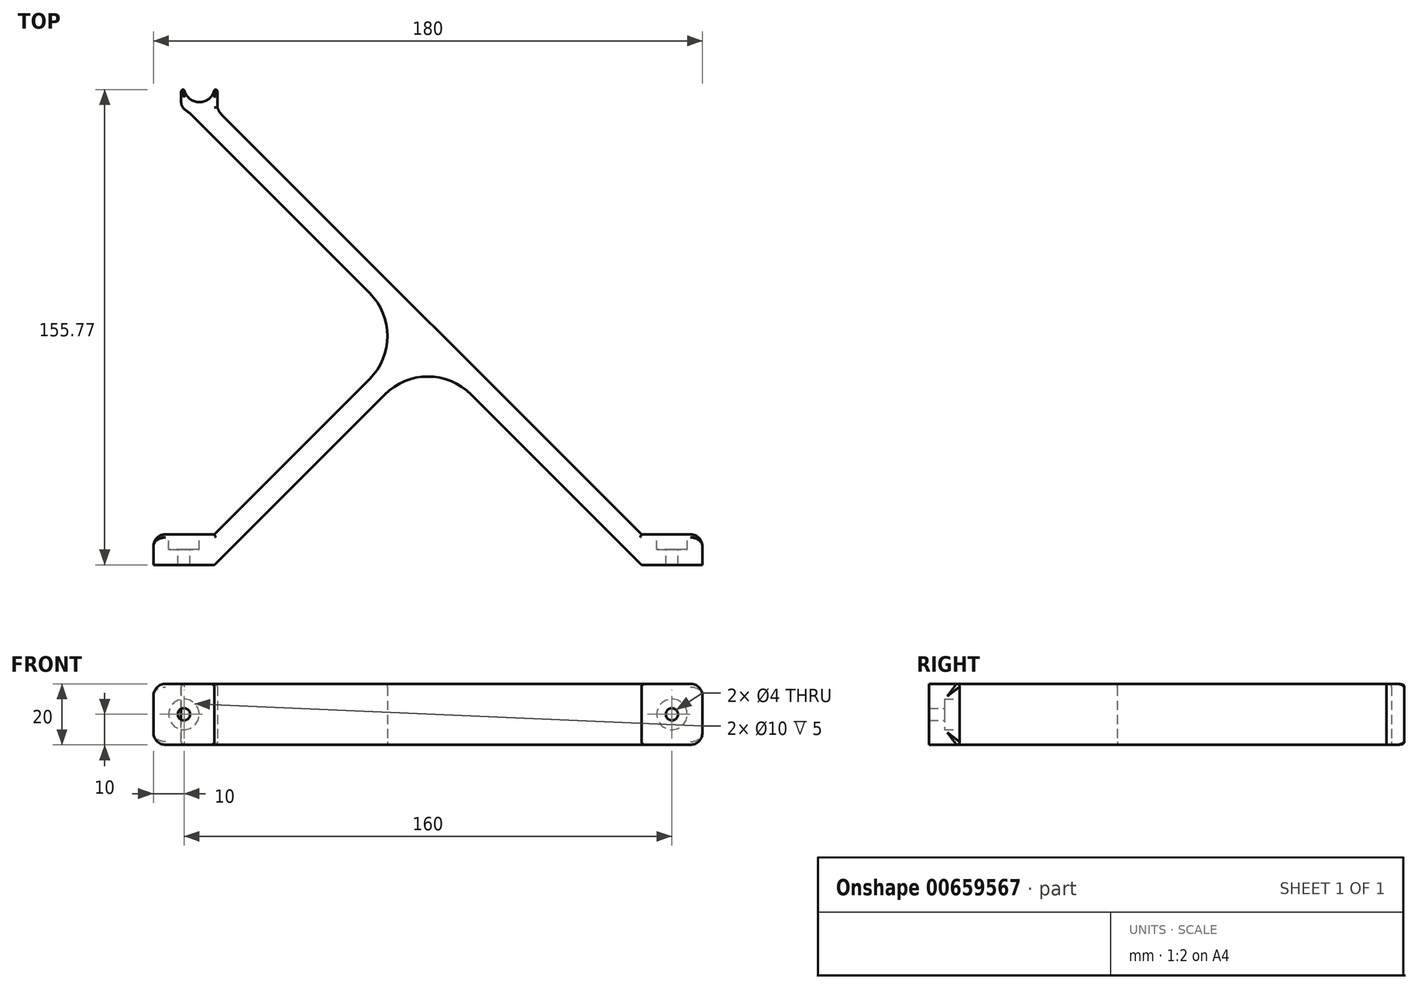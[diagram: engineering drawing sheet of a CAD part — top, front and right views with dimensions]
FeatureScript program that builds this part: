
annotation { "Feature Type Name" : "Feature", "Feature Type Description" : "" }
export const myFeature = defineFeature(function(context is Context, id is Id, definition is map)
    precondition{}
    {
        {
            var Q0;
            Q0=qCreatedBy(makeId("Top.planeOp"),FACE);
            var sketch = newSketch(context, id + "F0", { "sketchPlane" : qUnion([Q0])});
            skLineSegment(sketch, "E0", {"start": v(0, 0) * mm, "end": v(0, -75) * mm, "construction": true});
            skLineSegment(sketch, "E1", {"start": v(0, -75) * mm, "end": v(75, -75) * mm, "construction": true});
            skLineSegment(sketch, "E2", {"start": v(75, -75) * mm, "end": v(-74.9, 74.9) * mm});
            skLineSegment(sketch, "E3", {"start": v(0, 0) * mm, "end": v(-75, -75) * mm});
            skLineSegment(sketch, "E4", {"start": v(-147, -24.26) * mm, "end": v(-137, -24.26) * mm});
            skPoint(sketch, "E5", {"position": v(-142, -24.26) * mm});
            skLineSegment(sketch, "E6", {"start": v(-80, -75) * mm, "end": v(-70, -75) * mm});
            skPoint(sketch, "E7", {"position": v(-75, -75) * mm});
            skLineSegment(sketch, "E8", {"start": v(70, -75) * mm, "end": v(80, -75) * mm});
            skPoint(sketch, "E9", {"position": v(75, -75) * mm});
            skLineSegment(sketch, "E10", {"start": v(-5, -5) * mm, "end": v(5, -5) * mm});
            skPoint(sketch, "E11", {"position": v(0, -5) * mm});
            skLineSegment(sketch, "E12", {"start": v(-70, -75) * mm, "end": v(0, -5) * mm});
            skLineSegment(sketch, "E13", {"start": v(0, -5) * mm, "end": v(70, -75) * mm});
            skLineSegment(sketch, "E14", {"start": v(-5, 5) * mm, "end": v(-5, -5) * mm});
            skPoint(sketch, "E15", {"position": v(-5, 0) * mm});
            skLineSegment(sketch, "E16", {"start": v(-80, -75) * mm, "end": v(-5, 0) * mm});
            skLineSegment(sketch, "E17", {"start": v(80, -75) * mm, "end": v(-70, 75) * mm});
            skLineSegment(sketch, "E18", {"start": v(-70, 75) * mm, "end": v(-74.9, 74.9) * mm});
            skLineSegment(sketch, "E19", {"start": v(-74.9, 74.9) * mm, "end": v(-79.9, 74.9) * mm});
            skLineSegment(sketch, "E20", {"start": v(-79.9, 74.9) * mm, "end": v(-5, 0) * mm});
            skLineSegment(sketch, "E21", {"start": v(-5, 0) * mm, "end": v(-19.14, 14.14) * mm, "construction": true});
            skLineSegment(sketch, "E22", {"start": v(-5, 0) * mm, "end": v(-19.14, -14.14) * mm, "construction": true});
            skArc(sketch, "E23", {"start": v(-19.14, -14.14) * mm, "mid": v(-13.28, 0) * mm, "end": v(-19.14, 14.14) * mm});
            skLineSegment(sketch, "E24", {"start": v(0, -5) * mm, "end": v(-14.14, -19.14) * mm, "construction": true});
            skLineSegment(sketch, "E25", {"start": v(0, -5) * mm, "end": v(14.14, -19.14) * mm, "construction": true});
            skArc(sketch, "E26", {"start": v(14.14, -19.14) * mm, "mid": v(0, -13.28) * mm, "end": v(-14.14, -19.14) * mm});
            skLineSegment(sketch, "E27.bottom", {"start": v(-70, -75) * mm, "end": v(-90, -75) * mm});
            skLineSegment(sketch, "E27.top", {"start": v(-70, -65) * mm, "end": v(-90, -65) * mm});
            skLineSegment(sketch, "E27.left", {"start": v(-70, -75) * mm, "end": v(-70, -65) * mm});
            skLineSegment(sketch, "E27.right", {"start": v(-90, -75) * mm, "end": v(-90, -65) * mm});
            skLineSegment(sketch, "E28.bottom", {"start": v(70, -75) * mm, "end": v(90, -75) * mm});
            skLineSegment(sketch, "E28.top", {"start": v(70, -65) * mm, "end": v(90, -65) * mm});
            skLineSegment(sketch, "E28.left", {"start": v(70, -75) * mm, "end": v(70, -65) * mm});
            skLineSegment(sketch, "E28.right", {"start": v(90, -75) * mm, "end": v(90, -65) * mm});
            skArc(sketch, "E29", {"start": v(-79.9, 80.98) * mm, "mid": v(-74.95, 76.66) * mm, "end": v(-70, 80.98) * mm});
            skLineSegment(sketch, "E30", {"start": v(-79.9, 80.98) * mm, "end": v(-79.9, 74.9) * mm});
            skLineSegment(sketch, "E31", {"start": v(-70, 80.98) * mm, "end": v(-70, 75) * mm});
            skLineSegment(sketch, "E32", {"start": v(-79.9, 74.9) * mm, "end": v(-80.9, 74.9) * mm});
            skLineSegment(sketch, "E33", {"start": v(-80.9, 74.9) * mm, "end": v(-80.9, 80.98) * mm});
            skLineSegment(sketch, "E34", {"start": v(-79.9, 80.98) * mm, "end": v(-80.9, 80.98) * mm});
            skLineSegment(sketch, "E35", {"start": v(-70, 75) * mm, "end": v(-69, 75) * mm});
            skLineSegment(sketch, "E36", {"start": v(-69, 75) * mm, "end": v(-69, 80.98) * mm});
            skLineSegment(sketch, "E37", {"start": v(-69, 80.98) * mm, "end": v(-70, 80.98) * mm});
            skSolve(sketch);
        }
        {
            var Q0;
            {var subQ5=sQuery(id+"F0.wireOp",EDGE,"E12");Q0=makeQuery(id+"F0.imprint","IMPRINT",FACE,{"disambiguationData":[TD([[makeQuery(id+"F0.imprint","IMPRINT",EDGE,{"derivedFrom":subQ5}),1.0]])]});}
            var Q1;
            {var subQ5=sQuery(id+"F0.wireOp",EDGE,"E16");Q1=makeQuery(id+"F0.imprint","IMPRINT",FACE,{"disambiguationData":[TD([[makeQuery(id+"F0.imprint","IMPRINT",EDGE,{"derivedFrom":subQ5}),-1.0]])]});}
            var Q2;
            {var subQ5=sQuery(id+"F0.wireOp",EDGE,"E13");Q2=makeQuery(id+"F0.imprint","IMPRINT",FACE,{"disambiguationData":[TD([[makeQuery(id+"F0.imprint","IMPRINT",EDGE,{"derivedFrom":subQ5}),1.0]])]});}
            var Q3;
            {var subQ7=sQuery(id+"F0.wireOp",EDGE,"E17");Q3=makeQuery(id+"F0.imprint","IMPRINT",FACE,{"disambiguationData":[TD([[makeQuery(id+"F0.imprint","IMPRINT",EDGE,{"derivedFrom":subQ7}),1.0]])]});}
            var Q4;
            {var subQ0=sQuery(id+"F0.wireOp",EDGE,"E19");Q4=makeQuery(id+"F0.imprint","IMPRINT",FACE,{"disambiguationData":[TD([[makeQuery(id+"F0.imprint","IMPRINT",EDGE,{"derivedFrom":subQ0}),1.0]])]});}
            var Q5;
            {var subQ0=sQuery(id+"F0.wireOp",EDGE,"E3");var subQ1=sQuery(id+"F0.wireOp",EDGE,"E2");var subQ2=makeQuery(id+"F0.imprint","INTERSECT",VERTEX,{"derivedFrom":[subQ1,subQ0]});Q5=makeQuery(id+"F0.imprint","IMPRINT",FACE,{"disambiguationData":[TD([[makeQuery(id+"F0.imprint","IMPRINT",EDGE,{"disambiguationData":[TD([[subQ2,-1.0]])],"derivedFrom":subQ1}),1.0]])]});}
            var Q6;
            {var subQ0=sQuery(id+"F0.wireOp",EDGE,"E3");var subQ1=sQuery(id+"F0.wireOp",EDGE,"E2");var subQ2=makeQuery(id+"F0.imprint","INTERSECT",VERTEX,{"derivedFrom":[subQ1,subQ0]});Q6=makeQuery(id+"F0.imprint","IMPRINT",FACE,{"disambiguationData":[TD([[makeQuery(id+"F0.imprint","IMPRINT",EDGE,{"disambiguationData":[TD([[subQ2,1.0]])],"derivedFrom":subQ1}),1.0]])]});}
            var Q7;
            {var subQ3=sQuery(id+"F0.wireOp",EDGE,"E26");Q7=makeQuery(id+"F0.imprint","IMPRINT",FACE,{"disambiguationData":[TD([[makeQuery(id+"F0.imprint","IMPRINT",EDGE,{"derivedFrom":subQ3}),-1.0]])]});}
            var Q8;
            {var subQ3=sQuery(id+"F0.wireOp",EDGE,"E23");Q8=makeQuery(id+"F0.imprint","IMPRINT",FACE,{"disambiguationData":[TD([[makeQuery(id+"F0.imprint","IMPRINT",EDGE,{"derivedFrom":subQ3}),-1.0]])]});}
            var Q9;
            {var subQ3=sQuery(id+"F0.wireOp",EDGE,"E28.top");Q9=makeQuery(id+"F0.imprint","IMPRINT",FACE,{"disambiguationData":[TD([[makeQuery(id+"F0.imprint","IMPRINT",EDGE,{"derivedFrom":subQ3}),-1.0]])]});}
            var Q10;
            {var subQ0=sQuery(id+"F0.wireOp",EDGE,"E28.bottom");var subQ1=sQuery(id+"F0.wireOp",EDGE,"E2");var subQ2=makeQuery(id+"F0.imprint","INTERSECT",VERTEX,{"derivedFrom":[subQ1,subQ0]});Q10=makeQuery(id+"F0.imprint","IMPRINT",FACE,{"disambiguationData":[TD([[makeQuery(id+"F0.imprint","IMPRINT",EDGE,{"disambiguationData":[TD([[subQ2,-1.0]])],"derivedFrom":subQ1}),1.0]])]});}
            var Q11;
            {var subQ0=sQuery(id+"F0.wireOp",EDGE,"E18");Q11=makeQuery(id+"F0.imprint","IMPRINT",FACE,{"disambiguationData":[TD([[makeQuery(id+"F0.imprint","IMPRINT",EDGE,{"derivedFrom":subQ0}),1.0]])]});}
            var Q12;
            {var subQ0=sQuery(id+"F0.wireOp",EDGE,"E27.bottom");var subQ1=sQuery(id+"F0.wireOp",EDGE,"E3");var subQ2=makeQuery(id+"F0.imprint","INTERSECT",VERTEX,{"derivedFrom":[subQ1,subQ0]});Q12=makeQuery(id+"F0.imprint","IMPRINT",FACE,{"disambiguationData":[TD([[makeQuery(id+"F0.imprint","IMPRINT",EDGE,{"disambiguationData":[TD([[subQ2,1.0]])],"derivedFrom":subQ1}),-1.0]])]});}
            var Q13;
            {var subQ0=sQuery(id+"F0.wireOp",EDGE,"E27.bottom");var subQ1=sQuery(id+"F0.wireOp",EDGE,"E3");var subQ2=makeQuery(id+"F0.imprint","INTERSECT",VERTEX,{"derivedFrom":[subQ1,subQ0]});Q13=makeQuery(id+"F0.imprint","IMPRINT",FACE,{"disambiguationData":[TD([[makeQuery(id+"F0.imprint","IMPRINT",EDGE,{"disambiguationData":[TD([[subQ2,1.0]])],"derivedFrom":subQ1}),1.0]])]});}
            var Q14;
            {var subQ3=sQuery(id+"F0.wireOp",EDGE,"E27.top");Q14=makeQuery(id+"F0.imprint","IMPRINT",FACE,{"disambiguationData":[TD([[makeQuery(id+"F0.imprint","IMPRINT",EDGE,{"derivedFrom":subQ3}),1.0]])]});}
            var Q15;
            Q15=makeQuery(id+"F0.imprint","IMPRINT",FACE,{"disambiguationData":[TD([[makeQuery(id+"F0.imprint","IMPRINT",EDGE,{"derivedFrom":sQuery(id+"F0.wireOp",EDGE,"E18")}),-1.0]])]});
            var Q16;
            Q16=makeQuery(id+"F0.imprint","IMPRINT",FACE,{"disambiguationData":[TD([[makeQuery(id+"F0.imprint","IMPRINT",EDGE,{"derivedFrom":sQuery(id+"F0.wireOp",EDGE,"E30")}),-1.0]])]});
            var Q17;
            Q17=makeQuery(id+"F0.imprint","IMPRINT",FACE,{"disambiguationData":[TD([[makeQuery(id+"F0.imprint","IMPRINT",EDGE,{"derivedFrom":sQuery(id+"F0.wireOp",EDGE,"E31")}),1.0]])]});
            extrude(context, id + "F1", {"entities" : qUnion([Q0, Q1, Q2, Q3, Q4, Q5, Q6, Q7, Q8, Q9, Q10, Q11, Q12, Q13, Q14, Q15, Q16, Q17]), "endBound" : BoundingType.SYMMETRIC, "depth" : 20 * mm});
        }
        {
            var Q0;
            Q0=makeQuery(id+"F1.opExtrude","SWEPT_EDGE",EDGE,{"disambiguationData":[OSD([sQuery(id+"F0.wireOp",EDGE,"E19"),sQuery(id+"F0.wireOp",EDGE,"E20"),sQuery(id+"F0.wireOp",EDGE,"E30"),sQuery(id+"F0.wireOp",EDGE,"E32")])]});
            fillet(context, id + "F2", {"entities" : qUnion([Q0]), "radius" : 15 * mm, "tangentPropagation" : true, "allowEdgeOverflow" : false});
        }
        {
            var Q0;
            Q0=makeQuery(id+"F1.opExtrude","SWEPT_EDGE",EDGE,{"disambiguationData":[OSD([sQuery(id+"F0.wireOp",EDGE,"E17"),sQuery(id+"F0.wireOp",EDGE,"E18"),sQuery(id+"F0.wireOp",EDGE,"E31"),sQuery(id+"F0.wireOp",EDGE,"E35")])]});
            fillet(context, id + "F3", {"entities" : qUnion([Q0]), "radius" : 5 * mm, "tangentPropagation" : true, "allowEdgeOverflow" : false});
        }
        {
            var Q0;
            Q0=makeQuery(id+"F2.opFillet","BLEND_EDGE",EDGE,{"blendedFrom":[makeQuery(id+"F1.opExtrude","SWEPT_EDGE",EDGE,{"disambiguationData":[OSD([sQuery(id+"F0.wireOp",EDGE,"E19"),sQuery(id+"F0.wireOp",EDGE,"E20"),sQuery(id+"F0.wireOp",EDGE,"E30"),sQuery(id+"F0.wireOp",EDGE,"E32")])]}),makeQuery(id+"F1.opExtrude","SWEPT_FACE",FACE,{"disambiguationData":[OSD([sQuery(id+"F0.wireOp",EDGE,"E33")])]})],"blendedInto":[makeQuery(id+"F1.opExtrude","SWEPT_FACE",FACE,{"disambiguationData":[OSD([sQuery(id+"F0.wireOp",EDGE,"E33")])]})]});
            fillet(context, id + "F4", {"entities" : qUnion([Q0]), "radius" : 3 * mm, "tangentPropagation" : true, "allowEdgeOverflow" : false});
        }
        {
            var Q0;
            Q0=makeQuery(id+"F1.opExtrude","SWEPT_FACE",FACE,{"disambiguationData":[OSD([sQuery(id+"F0.wireOp",EDGE,"E27.top")])]});
            var sketch = newSketch(context, id + "F5", { "sketchPlane" : qUnion([Q0])});
            skPoint(sketch, "E38", {"position": v(80, 0) * mm});
            skPoint(sketch, "E38.positionSnap0", {"position": v(80, -10) * mm});
            skPoint(sketch, "E38.positionSnap1", {"position": v(90, 0) * mm});
            skCircle(sketch, "E39", {"center": v(80, 0) * mm, "radius": 5 * mm});
            skCircle(sketch, "E40", {"center": v(80, 0) * mm, "radius": 2 * mm});
            skSolve(sketch);
        }
        {
            var Q0;
            Q0=makeQuery(id+"F1.opExtrude","SWEPT_FACE",FACE,{"disambiguationData":[OSD([sQuery(id+"F0.wireOp",EDGE,"E28.top")])]});
            var sketch = newSketch(context, id + "F6", { "sketchPlane" : qUnion([Q0])});
            skPoint(sketch, "E41", {"position": v(-80, 0) * mm});
            skPoint(sketch, "E41.positionSnap0", {"position": v(-80, 10) * mm});
            skPoint(sketch, "E41.positionSnap1", {"position": v(-70, 0) * mm});
            skPoint(sketch, "E42.positionSnap0", {"position": v(-80, -8.37) * mm});
            skPoint(sketch, "E42.positionSnap1", {"position": v(-77.63, 0) * mm});
            skCircle(sketch, "E43", {"center": v(-80, 0) * mm, "radius": 5 * mm});
            skCircle(sketch, "E44", {"center": v(-80, 0) * mm, "radius": 2 * mm});
            skSolve(sketch);
        }
        {
            var Q0;
            Q0=makeQuery(id+"F5.imprint","IMPRINT",FACE,{"disambiguationData":[TD([[makeQuery(id+"F5.imprint","IMPRINT",EDGE,{"derivedFrom":sQuery(id+"F5.wireOp",EDGE,"E40")}),1.0]])]});
            var Q1;
            Q1=makeQuery(id+"F6.imprint","IMPRINT",FACE,{"disambiguationData":[TD([[makeQuery(id+"F6.imprint","IMPRINT",EDGE,{"derivedFrom":sQuery(id+"F6.wireOp",EDGE,"E44")}),1.0]])]});
            extrude(context, id + "F7", {"entities" : qUnion([Q0, Q1]), "operationType" : NewBodyOperationType.REMOVE, "oppositeDirection" : true, "depth" : 25 * mm});
        }
        {
            var Q0;
            Q0=makeQuery(id+"F5.imprint","IMPRINT",FACE,{"disambiguationData":[TD([[makeQuery(id+"F5.imprint","IMPRINT",EDGE,{"derivedFrom":sQuery(id+"F5.wireOp",EDGE,"E39")}),1.0]])]});
            var Q1;
            Q1=qSketchRegion(id+"F6",true);
            extrude(context, id + "F8", {"entities" : qUnion([Q0, Q1]), "operationType" : NewBodyOperationType.REMOVE, "oppositeDirection" : true, "depth" : 5 * mm});
        }
        {
            var Q0;
            Q0=makeQuery(id+"F1.opExtrude","SWEPT_EDGE",EDGE,{"disambiguationData":[OSD([sQuery(id+"F0.wireOp",EDGE,"E27.top"),sQuery(id+"F0.wireOp",EDGE,"E27.right")])]});
            var Q1;
            Q1=makeQuery(id+"F1.opExtrude","CAP_EDGE",EDGE,{"disambiguationData":[OSD([sQuery(id+"F0.wireOp",EDGE,"E27.right")])],"isStart":false});
            var Q2;
            Q2=makeQuery(id+"F1.opExtrude","CAP_EDGE",EDGE,{"disambiguationData":[OSD([sQuery(id+"F0.wireOp",EDGE,"E27.right")])],"isStart":true});
            var Q3;
            Q3=makeQuery(id+"F1.opExtrude","CAP_EDGE",EDGE,{"disambiguationData":[OSD([sQuery(id+"F0.wireOp",EDGE,"E28.right")])],"isStart":false});
            var Q4;
            Q4=makeQuery(id+"F1.opExtrude","CAP_EDGE",EDGE,{"disambiguationData":[OSD([sQuery(id+"F0.wireOp",EDGE,"E28.right")])],"isStart":true});
            var Q5;
            Q5=makeQuery(id+"F1.opExtrude","SWEPT_EDGE",EDGE,{"disambiguationData":[OSD([sQuery(id+"F0.wireOp",EDGE,"E28.top"),sQuery(id+"F0.wireOp",EDGE,"E28.right")])]});
            fillet(context, id + "F9", {"entities" : qUnion([Q0, Q1, Q2, Q3, Q4, Q5]), "radius" : 4 * mm, "tangentPropagation" : true, "allowEdgeOverflow" : false});
        }
        {
            var Q0;
            Q0=makeQuery(id+"F1.opExtrude","CAP_EDGE",EDGE,{"disambiguationData":[OSD([sQuery(id+"F0.wireOp",EDGE,"E28.top")])],"isStart":true});
            var Q1;
            Q1=makeQuery(id+"F1.opExtrude","CAP_EDGE",EDGE,{"disambiguationData":[OSD([sQuery(id+"F0.wireOp",EDGE,"E28.top")])],"isStart":false});
            var Q2;
            Q2=makeQuery(id+"F1.opExtrude","CAP_EDGE",EDGE,{"disambiguationData":[OSD([sQuery(id+"F0.wireOp",EDGE,"E17")])],"isStart":true});
            var Q3;
            Q3=makeQuery(id+"F1.opExtrude","CAP_EDGE",EDGE,{"disambiguationData":[OSD([sQuery(id+"F0.wireOp",EDGE,"E17")])],"isStart":false});
            var Q4;
            Q4=makeQuery(id+"F1.opExtrude","CAP_EDGE",EDGE,{"disambiguationData":[OSD([sQuery(id+"F0.wireOp",EDGE,"E27.top")])],"isStart":true});
            var Q5;
            Q5=makeQuery(id+"F1.opExtrude","CAP_EDGE",EDGE,{"disambiguationData":[OSD([sQuery(id+"F0.wireOp",EDGE,"E27.top")])],"isStart":false});
            var Q6;
            Q6=makeQuery(id+"F1.opExtrude","CAP_EDGE",EDGE,{"disambiguationData":[OSD([sQuery(id+"F0.wireOp",EDGE,"E13")])],"isStart":true});
            var Q7;
            Q7=makeQuery(id+"F1.opExtrude","CAP_EDGE",EDGE,{"disambiguationData":[OSD([sQuery(id+"F0.wireOp",EDGE,"E13")])],"isStart":false});
            fillet(context, id + "F10", {"entities" : qUnion([Q0, Q1, Q2, Q3, Q4, Q5, Q6, Q7]), "radius" : 1 * mm, "tangentPropagation" : true, "allowEdgeOverflow" : false});
        }
        {
            var Q0;
            Q0=makeQuery(id+"F1.opExtrude","SWEPT_EDGE",EDGE,{"disambiguationData":[OSD([sQuery(id+"F0.wireOp",EDGE,"E29"),sQuery(id+"F0.wireOp",EDGE,"E31"),sQuery(id+"F0.wireOp",EDGE,"E37")])]});
            var Q1;
            Q1=makeQuery(id+"F1.opExtrude","SWEPT_EDGE",EDGE,{"disambiguationData":[OSD([sQuery(id+"F0.wireOp",EDGE,"E36"),sQuery(id+"F0.wireOp",EDGE,"E37")])]});
            var Q2;
            Q2=makeQuery(id+"F1.opExtrude","SWEPT_EDGE",EDGE,{"disambiguationData":[OSD([sQuery(id+"F0.wireOp",EDGE,"E29"),sQuery(id+"F0.wireOp",EDGE,"E30"),sQuery(id+"F0.wireOp",EDGE,"E34")])]});
            var Q3;
            Q3=makeQuery(id+"F1.opExtrude","SWEPT_EDGE",EDGE,{"disambiguationData":[OSD([sQuery(id+"F0.wireOp",EDGE,"E33"),sQuery(id+"F0.wireOp",EDGE,"E34")])]});
            fillet(context, id + "F11", {"entities" : qUnion([Q0, Q1, Q2, Q3]), "radius" : 1 * mm, "tangentPropagation" : true, "allowEdgeOverflow" : false});
        }
        {
            var Q0;
            {var subQ0=sQuery(id+"F0.wireOp",EDGE,"E37");Q0=makeQuery(id+"F11.opFillet","BLEND_EDGE",EDGE,{"blendedFrom":[makeQuery(id+"F1.opExtrude","SWEPT_EDGE",EDGE,{"disambiguationData":[OSD([sQuery(id+"F0.wireOp",EDGE,"E29"),sQuery(id+"F0.wireOp",EDGE,"E31"),subQ0])]}),makeQuery(id+"F1.opExtrude","SWEPT_EDGE",EDGE,{"disambiguationData":[OSD([sQuery(id+"F0.wireOp",EDGE,"E36"),subQ0])]})],"blendedInto":[]});}
            var Q1;
            {var subQ0=sQuery(id+"F0.wireOp",EDGE,"E34");Q1=makeQuery(id+"F11.opFillet","BLEND_EDGE",EDGE,{"blendedFrom":[makeQuery(id+"F1.opExtrude","SWEPT_EDGE",EDGE,{"disambiguationData":[OSD([sQuery(id+"F0.wireOp",EDGE,"E29"),sQuery(id+"F0.wireOp",EDGE,"E30"),subQ0])]}),makeQuery(id+"F1.opExtrude","SWEPT_EDGE",EDGE,{"disambiguationData":[OSD([sQuery(id+"F0.wireOp",EDGE,"E33"),subQ0])]})],"blendedInto":[]});}
            fillet(context, id + "F12", {"entities" : qUnion([Q0, Q1]), "radius" : .5 * mm, "tangentPropagation" : true, "allowEdgeOverflow" : false});
        }
        {
            var Q0;
            Q0=makeQuery(id+"F1.opExtrude","CAP_EDGE",EDGE,{"disambiguationData":[OSD([sQuery(id+"F0.wireOp",EDGE,"E36")])],"isStart":true});
            var Q1;
            Q1=makeQuery(id+"F1.opExtrude","CAP_EDGE",EDGE,{"disambiguationData":[OSD([sQuery(id+"F0.wireOp",EDGE,"E36")])],"isStart":false});
            var Q2;
            Q2=makeQuery(id+"F1.opExtrude","CAP_EDGE",EDGE,{"disambiguationData":[OSD([sQuery(id+"F0.wireOp",EDGE,"E33")])],"isStart":true});
            var Q3;
            {var subQ0=sQuery(id+"F0.wireOp",EDGE,"E33");var subQ1=sQuery(id+"F0.wireOp",EDGE,"E32");var subQ2=sQuery(id+"F0.wireOp",EDGE,"E20");Q3=makeQuery(id+"F4.opFillet","BLEND_EDGE",EDGE,{"blendedFrom":[makeQuery(id+"F2.opFillet","BLEND_EDGE",EDGE,{"blendedFrom":[makeQuery(id+"F1.opExtrude","SWEPT_EDGE",EDGE,{"disambiguationData":[OSD([sQuery(id+"F0.wireOp",EDGE,"E19"),subQ2,sQuery(id+"F0.wireOp",EDGE,"E30"),subQ1])]}),makeQuery(id+"F1.opExtrude","SWEPT_FACE",FACE,{"disambiguationData":[OSD([subQ0])]})],"blendedInto":[makeQuery(id+"F1.opExtrude","SWEPT_FACE",FACE,{"disambiguationData":[OSD([subQ0])]})]}),makeQuery(id+"F1.opExtrude","CAP_FACE",FACE,{"disambiguationData":[OSD([sQuery(id+"F0.wireOp",EDGE,"E12"),sQuery(id+"F0.wireOp",EDGE,"E13"),sQuery(id+"F0.wireOp",EDGE,"E16"),sQuery(id+"F0.wireOp",EDGE,"E17"),subQ2,sQuery(id+"F0.wireOp",EDGE,"E23"),sQuery(id+"F0.wireOp",EDGE,"E26"),sQuery(id+"F0.wireOp",EDGE,"E27.bottom"),sQuery(id+"F0.wireOp",EDGE,"E27.top"),sQuery(id+"F0.wireOp",EDGE,"E27.right"),sQuery(id+"F0.wireOp",EDGE,"E28.bottom"),sQuery(id+"F0.wireOp",EDGE,"E28.top"),sQuery(id+"F0.wireOp",EDGE,"E28.right"),sQuery(id+"F0.wireOp",EDGE,"E29"),subQ1,subQ0,sQuery(id+"F0.wireOp",EDGE,"E34"),sQuery(id+"F0.wireOp",EDGE,"E35"),sQuery(id+"F0.wireOp",EDGE,"E36"),sQuery(id+"F0.wireOp",EDGE,"E37")])],"isStart":true})],"blendedInto":[makeQuery(id+"F1.opExtrude","CAP_FACE",FACE,{"disambiguationData":[OSD([sQuery(id+"F0.wireOp",EDGE,"E12"),sQuery(id+"F0.wireOp",EDGE,"E13"),sQuery(id+"F0.wireOp",EDGE,"E16"),sQuery(id+"F0.wireOp",EDGE,"E17"),subQ2,sQuery(id+"F0.wireOp",EDGE,"E23"),sQuery(id+"F0.wireOp",EDGE,"E26"),sQuery(id+"F0.wireOp",EDGE,"E27.bottom"),sQuery(id+"F0.wireOp",EDGE,"E27.top"),sQuery(id+"F0.wireOp",EDGE,"E27.right"),sQuery(id+"F0.wireOp",EDGE,"E28.bottom"),sQuery(id+"F0.wireOp",EDGE,"E28.top"),sQuery(id+"F0.wireOp",EDGE,"E28.right"),sQuery(id+"F0.wireOp",EDGE,"E29"),subQ1,subQ0,sQuery(id+"F0.wireOp",EDGE,"E34"),sQuery(id+"F0.wireOp",EDGE,"E35"),sQuery(id+"F0.wireOp",EDGE,"E36"),sQuery(id+"F0.wireOp",EDGE,"E37")])],"isStart":true})]});}
            var Q4;
            Q4=makeQuery(id+"F1.opExtrude","CAP_EDGE",EDGE,{"disambiguationData":[OSD([sQuery(id+"F0.wireOp",EDGE,"E33")])],"isStart":false});
            var Q5;
            {var subQ0=sQuery(id+"F0.wireOp",EDGE,"E33");var subQ1=sQuery(id+"F0.wireOp",EDGE,"E32");var subQ2=sQuery(id+"F0.wireOp",EDGE,"E20");Q5=makeQuery(id+"F4.opFillet","BLEND_EDGE",EDGE,{"blendedFrom":[makeQuery(id+"F2.opFillet","BLEND_EDGE",EDGE,{"blendedFrom":[makeQuery(id+"F1.opExtrude","SWEPT_EDGE",EDGE,{"disambiguationData":[OSD([sQuery(id+"F0.wireOp",EDGE,"E19"),subQ2,sQuery(id+"F0.wireOp",EDGE,"E30"),subQ1])]}),makeQuery(id+"F1.opExtrude","SWEPT_FACE",FACE,{"disambiguationData":[OSD([subQ0])]})],"blendedInto":[makeQuery(id+"F1.opExtrude","SWEPT_FACE",FACE,{"disambiguationData":[OSD([subQ0])]})]}),makeQuery(id+"F1.opExtrude","CAP_FACE",FACE,{"disambiguationData":[OSD([sQuery(id+"F0.wireOp",EDGE,"E12"),sQuery(id+"F0.wireOp",EDGE,"E13"),sQuery(id+"F0.wireOp",EDGE,"E16"),sQuery(id+"F0.wireOp",EDGE,"E17"),subQ2,sQuery(id+"F0.wireOp",EDGE,"E23"),sQuery(id+"F0.wireOp",EDGE,"E26"),sQuery(id+"F0.wireOp",EDGE,"E27.bottom"),sQuery(id+"F0.wireOp",EDGE,"E27.top"),sQuery(id+"F0.wireOp",EDGE,"E27.right"),sQuery(id+"F0.wireOp",EDGE,"E28.bottom"),sQuery(id+"F0.wireOp",EDGE,"E28.top"),sQuery(id+"F0.wireOp",EDGE,"E28.right"),sQuery(id+"F0.wireOp",EDGE,"E29"),subQ1,subQ0,sQuery(id+"F0.wireOp",EDGE,"E34"),sQuery(id+"F0.wireOp",EDGE,"E35"),sQuery(id+"F0.wireOp",EDGE,"E36"),sQuery(id+"F0.wireOp",EDGE,"E37")])],"isStart":false})],"blendedInto":[makeQuery(id+"F1.opExtrude","CAP_FACE",FACE,{"disambiguationData":[OSD([sQuery(id+"F0.wireOp",EDGE,"E12"),sQuery(id+"F0.wireOp",EDGE,"E13"),sQuery(id+"F0.wireOp",EDGE,"E16"),sQuery(id+"F0.wireOp",EDGE,"E17"),subQ2,sQuery(id+"F0.wireOp",EDGE,"E23"),sQuery(id+"F0.wireOp",EDGE,"E26"),sQuery(id+"F0.wireOp",EDGE,"E27.bottom"),sQuery(id+"F0.wireOp",EDGE,"E27.top"),sQuery(id+"F0.wireOp",EDGE,"E27.right"),sQuery(id+"F0.wireOp",EDGE,"E28.bottom"),sQuery(id+"F0.wireOp",EDGE,"E28.top"),sQuery(id+"F0.wireOp",EDGE,"E28.right"),sQuery(id+"F0.wireOp",EDGE,"E29"),subQ1,subQ0,sQuery(id+"F0.wireOp",EDGE,"E34"),sQuery(id+"F0.wireOp",EDGE,"E35"),sQuery(id+"F0.wireOp",EDGE,"E36"),sQuery(id+"F0.wireOp",EDGE,"E37")])],"isStart":false})]});}
            var Q6;
            {var subQ0=sQuery(id+"F0.wireOp",EDGE,"E32");var subQ1=sQuery(id+"F0.wireOp",EDGE,"E20");Q6=makeQuery(id+"F2.opFillet","BLEND_EDGE",EDGE,{"blendedFrom":[makeQuery(id+"F1.opExtrude","SWEPT_EDGE",EDGE,{"disambiguationData":[OSD([sQuery(id+"F0.wireOp",EDGE,"E19"),subQ1,sQuery(id+"F0.wireOp",EDGE,"E30"),subQ0])]}),makeQuery(id+"F1.opExtrude","CAP_FACE",FACE,{"disambiguationData":[OSD([sQuery(id+"F0.wireOp",EDGE,"E12"),sQuery(id+"F0.wireOp",EDGE,"E13"),sQuery(id+"F0.wireOp",EDGE,"E16"),sQuery(id+"F0.wireOp",EDGE,"E17"),subQ1,sQuery(id+"F0.wireOp",EDGE,"E23"),sQuery(id+"F0.wireOp",EDGE,"E26"),sQuery(id+"F0.wireOp",EDGE,"E27.bottom"),sQuery(id+"F0.wireOp",EDGE,"E27.top"),sQuery(id+"F0.wireOp",EDGE,"E27.right"),sQuery(id+"F0.wireOp",EDGE,"E28.bottom"),sQuery(id+"F0.wireOp",EDGE,"E28.top"),sQuery(id+"F0.wireOp",EDGE,"E28.right"),sQuery(id+"F0.wireOp",EDGE,"E29"),subQ0,sQuery(id+"F0.wireOp",EDGE,"E33"),sQuery(id+"F0.wireOp",EDGE,"E34"),sQuery(id+"F0.wireOp",EDGE,"E35"),sQuery(id+"F0.wireOp",EDGE,"E36"),sQuery(id+"F0.wireOp",EDGE,"E37")])],"isStart":false})],"blendedInto":[makeQuery(id+"F1.opExtrude","CAP_FACE",FACE,{"disambiguationData":[OSD([sQuery(id+"F0.wireOp",EDGE,"E12"),sQuery(id+"F0.wireOp",EDGE,"E13"),sQuery(id+"F0.wireOp",EDGE,"E16"),sQuery(id+"F0.wireOp",EDGE,"E17"),subQ1,sQuery(id+"F0.wireOp",EDGE,"E23"),sQuery(id+"F0.wireOp",EDGE,"E26"),sQuery(id+"F0.wireOp",EDGE,"E27.bottom"),sQuery(id+"F0.wireOp",EDGE,"E27.top"),sQuery(id+"F0.wireOp",EDGE,"E27.right"),sQuery(id+"F0.wireOp",EDGE,"E28.bottom"),sQuery(id+"F0.wireOp",EDGE,"E28.top"),sQuery(id+"F0.wireOp",EDGE,"E28.right"),sQuery(id+"F0.wireOp",EDGE,"E29"),subQ0,sQuery(id+"F0.wireOp",EDGE,"E33"),sQuery(id+"F0.wireOp",EDGE,"E34"),sQuery(id+"F0.wireOp",EDGE,"E35"),sQuery(id+"F0.wireOp",EDGE,"E36"),sQuery(id+"F0.wireOp",EDGE,"E37")])],"isStart":false})]});}
            var Q7;
            {var subQ0=sQuery(id+"F0.wireOp",EDGE,"E32");var subQ1=sQuery(id+"F0.wireOp",EDGE,"E20");Q7=makeQuery(id+"F2.opFillet","BLEND_EDGE",EDGE,{"blendedFrom":[makeQuery(id+"F1.opExtrude","SWEPT_EDGE",EDGE,{"disambiguationData":[OSD([sQuery(id+"F0.wireOp",EDGE,"E19"),subQ1,sQuery(id+"F0.wireOp",EDGE,"E30"),subQ0])]}),makeQuery(id+"F1.opExtrude","CAP_FACE",FACE,{"disambiguationData":[OSD([sQuery(id+"F0.wireOp",EDGE,"E12"),sQuery(id+"F0.wireOp",EDGE,"E13"),sQuery(id+"F0.wireOp",EDGE,"E16"),sQuery(id+"F0.wireOp",EDGE,"E17"),subQ1,sQuery(id+"F0.wireOp",EDGE,"E23"),sQuery(id+"F0.wireOp",EDGE,"E26"),sQuery(id+"F0.wireOp",EDGE,"E27.bottom"),sQuery(id+"F0.wireOp",EDGE,"E27.top"),sQuery(id+"F0.wireOp",EDGE,"E27.right"),sQuery(id+"F0.wireOp",EDGE,"E28.bottom"),sQuery(id+"F0.wireOp",EDGE,"E28.top"),sQuery(id+"F0.wireOp",EDGE,"E28.right"),sQuery(id+"F0.wireOp",EDGE,"E29"),subQ0,sQuery(id+"F0.wireOp",EDGE,"E33"),sQuery(id+"F0.wireOp",EDGE,"E34"),sQuery(id+"F0.wireOp",EDGE,"E35"),sQuery(id+"F0.wireOp",EDGE,"E36"),sQuery(id+"F0.wireOp",EDGE,"E37")])],"isStart":true})],"blendedInto":[makeQuery(id+"F1.opExtrude","CAP_FACE",FACE,{"disambiguationData":[OSD([sQuery(id+"F0.wireOp",EDGE,"E12"),sQuery(id+"F0.wireOp",EDGE,"E13"),sQuery(id+"F0.wireOp",EDGE,"E16"),sQuery(id+"F0.wireOp",EDGE,"E17"),subQ1,sQuery(id+"F0.wireOp",EDGE,"E23"),sQuery(id+"F0.wireOp",EDGE,"E26"),sQuery(id+"F0.wireOp",EDGE,"E27.bottom"),sQuery(id+"F0.wireOp",EDGE,"E27.top"),sQuery(id+"F0.wireOp",EDGE,"E27.right"),sQuery(id+"F0.wireOp",EDGE,"E28.bottom"),sQuery(id+"F0.wireOp",EDGE,"E28.top"),sQuery(id+"F0.wireOp",EDGE,"E28.right"),sQuery(id+"F0.wireOp",EDGE,"E29"),subQ0,sQuery(id+"F0.wireOp",EDGE,"E33"),sQuery(id+"F0.wireOp",EDGE,"E34"),sQuery(id+"F0.wireOp",EDGE,"E35"),sQuery(id+"F0.wireOp",EDGE,"E36"),sQuery(id+"F0.wireOp",EDGE,"E37")])],"isStart":true})]});}
            fillet(context, id + "F13", {"entities" : qUnion([Q0, Q1, Q2, Q3, Q4, Q5, Q6, Q7]), "radius" : 1 * mm, "tangentPropagation" : true, "allowEdgeOverflow" : false});
        }
    });
